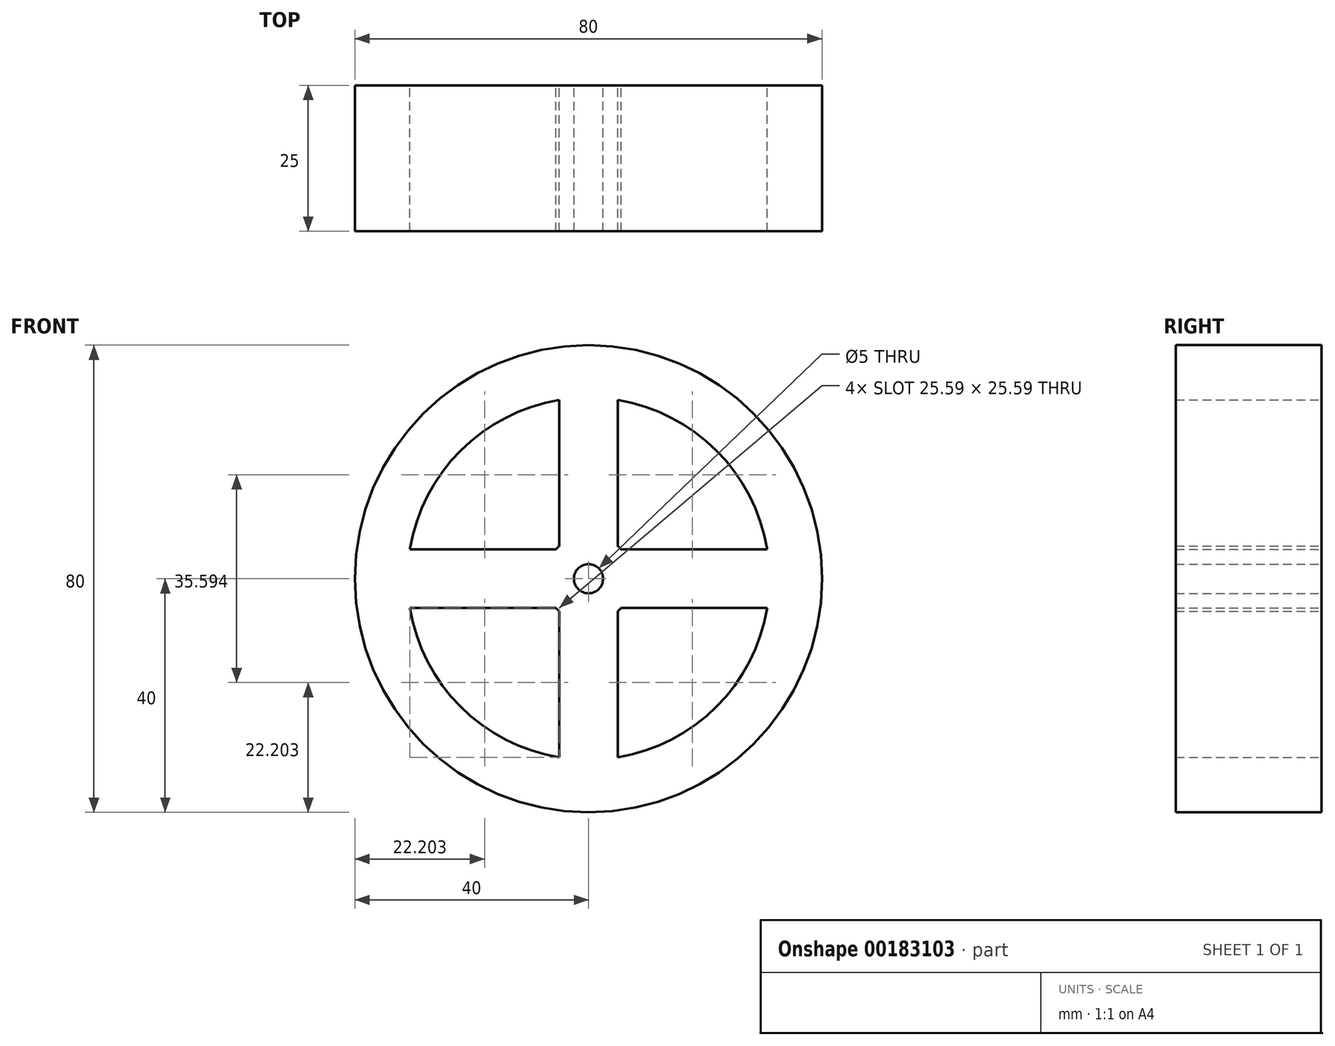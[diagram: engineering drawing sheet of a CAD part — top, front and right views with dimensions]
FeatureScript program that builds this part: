
annotation { "Feature Type Name" : "Feature", "Feature Type Description" : "" }
export const myFeature = defineFeature(function(context is Context, id is Id, definition is map)
    precondition{}
    {
        {
            var Q0;
            Q0=qCreatedBy(makeId("Front.planeOp"),FACE);
            var sketch = newSketch(context, id + "F0", { "sketchPlane" : qUnion([Q0])});
            skCircle(sketch, "E0", {"center": v(0, 0) * mm, "radius": 40 * mm});
            skArc(sketch, "E1", {"start": v(-30.6, -5) * mm, "mid": v(-21.92, -21.92) * mm, "end": v(-5, -30.6) * mm});
            skArc(sketch, "E2", {"start": v(5, -5.6) * mm, "mid": v(5.3, -5.3) * mm, "end": v(5.6, -5) * mm});
            skCircle(sketch, "E3", {"center": v(0, 0) * mm, "radius": 2.5 * mm});
            skLineSegment(sketch, "E4", {"start": v(0, 0) * mm, "end": v(0, 2.5) * mm, "construction": true});
            skLineSegment(sketch, "E5", {"start": v(0, 0) * mm, "end": v(0, -31) * mm, "construction": true});
            skLineSegment(sketch, "E6", {"start": v(0, 0) * mm, "end": v(31, 0) * mm, "construction": true});
            skLineSegment(sketch, "E7", {"start": v(0, 0) * mm, "end": v(-31, 0) * mm, "construction": true});
            skLineSegment(sketch, "E8.0", {"start": v(-5, 5.6) * mm, "end": v(-5, 30.6) * mm});
            skLineSegment(sketch, "E9.0", {"start": v(5, 5.6) * mm, "end": v(5, 30.6) * mm});
            skLineSegment(sketch, "E10.0", {"start": v(-5.6, 5) * mm, "end": v(-30.6, 5) * mm});
            skLineSegment(sketch, "E11.0", {"start": v(-5.6, -5) * mm, "end": v(-30.6, -5) * mm});
            skLineSegment(sketch, "E12.0", {"start": v(5.6, -5) * mm, "end": v(30.6, -5) * mm});
            skLineSegment(sketch, "E13.0", {"start": v(5, -5.6) * mm, "end": v(5, -30.6) * mm});
            skLineSegment(sketch, "E14.0", {"start": v(-5, -5.6) * mm, "end": v(-5, -30.6) * mm});
            skArc(sketch, "E15.trimOffspring", {"start": v(5, -30.6) * mm, "mid": v(21.92, -21.92) * mm, "end": v(30.6, -5) * mm});
            skArc(sketch, "E16.trimOffspring", {"start": v(30.6, 5) * mm, "mid": v(21.92, 21.92) * mm, "end": v(5, 30.6) * mm});
            skArc(sketch, "E17.trimOffspring", {"start": v(-5, 30.6) * mm, "mid": v(-21.92, 21.92) * mm, "end": v(-30.6, 5) * mm});
            skArc(sketch, "E18.trimOffspring", {"start": v(5.6, 5) * mm, "mid": v(5.3, 5.3) * mm, "end": v(5, 5.6) * mm});
            skArc(sketch, "E19.trimOffspring", {"start": v(-5.6, -5) * mm, "mid": v(-5.3, -5.3) * mm, "end": v(-5, -5.6) * mm});
            skArc(sketch, "E20.trimOffspring", {"start": v(-5, 5.6) * mm, "mid": v(-5.3, 5.3) * mm, "end": v(-5.6, 5) * mm});
            skLineSegment(sketch, "E21.trimOffspring", {"start": v(5.6, 5) * mm, "end": v(30.6, 5) * mm});
            skLineSegment(sketch, "E22.trimOffspring", {"start": v(0, 5) * mm, "end": v(0, 31) * mm, "construction": true});
            skSolve(sketch);
        }
        {
            var Q0;
            Q0 = qSketchRegion(id + "F0", true);
            extrude(context, id + "F1", {"entities" : qUnion([Q0]), "depth" : 25 * mm});
        }
    });
